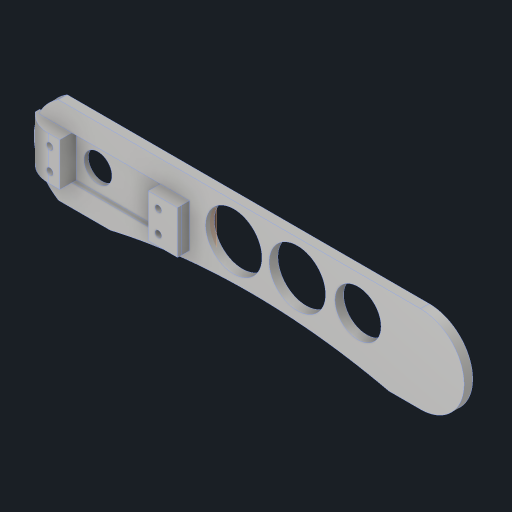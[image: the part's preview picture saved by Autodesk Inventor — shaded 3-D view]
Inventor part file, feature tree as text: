
AUTODESK INVENTOR PART (.ipt)
format: ipt  version: 2023.4 (Build 274418000, 418)  size: 249,344 bytes
history: native  units: mm
features: sketch x17, extrude x12, plane x1, fillet x1
ambient origin geometry x8: Origin, YZ Plane, XZ Plane, XY Plane, X Axis, Y Axis, Z Axis, Center Point
bodies: Solid1 (feature_tree)
feature tree (31):
  extrude  "Extrusion1"  Depth=20.0mm
  extrude  "Extrusion2"  Depth=4.0mm
  extrude  "Extrusion5"  Depth=11.9mm TaperAngle=0.0deg
  sketch  "Sketch6"  dims[d5=8.0mm d6=11.9mm d7=0.0mm]
  extrude  "Extrusion6"  Depth=10.0mm
  sketch  "Sketch8"  dims[d19=5.0mm d20=0.0mm d21=11.9mm d22=0.0mm]
  extrude  "Extrusion7"  Depth=11.9mm TaperAngle=0.0deg
  sketch  "Sketch9"  dims[d23=70.753mm d24=19.8mm]
  sketch  "Sketch10"  dims[d25=26.749mm d26=9.9mm]
  sketch  "Sketch11"  dims[d29=4.0mm d30=0.0mm d31=2.0mm d32=0.0mm d33=19.8mm]
  sketch  "Sketch12"  dims[d34=16.749mm d35=10.0mm]
  plane  "Work Plane1"
  extrude  "Extrusion9"  Depth=19.8mm
  extrude  "Extrusion10"  Depth=9.9mm
  extrude  "Extrusion11"  Depth=4.0mm TaperAngle=0.0deg
  fillet  "Fillet3"  Radius=19.8mm
  extrude  "Extrusion12"  Depth=10.0mm
  extrude  "Extrusion13"  Depth=19.8mm
  sketch  "Sketch17"  dims[d45=2.95mm]
  sketch  "Sketch18"  dims[d47=4.9mm]
  extrude  "Extrusion14"  Depth=7.5mm TaperAngle=0.0deg
  extrude  "Extrusion15"  Depth=5.5mm TaperAngle=0.0deg
  sketch  "Sketch20"  dims[d50=2.95mm d51=2.95mm d52=4.59mm d53=4.59mm d54=4.9mm d55=4.9mm d56=10.0mm d57=0.0mm d58=11.9mm d59=0.0mm d60=14.59mm d61=14.59mm d62=10.0mm d63=0.0mm]
  sketch  "Sketch1"  dims[d0=150.0mm d1=20.0mm]
  sketch  "Sketch5"  dims[d2=4.0mm d3=0.0mm d4=12.8mm]
  sketch  "Sketch7"  dims[d16=10.0mm d17=0.0mm d18=5.4mm]
  sketch  "Sketch13"  dims[d36=13.4mm d37=19.8mm]
  sketch  "Sketch14"  dims[d38=30.6mm d39=7.5mm d40=0.0mm]
  sketch  "Sketch15"  dims[d41=14.75mm d42=5.5mm d43=0.0mm]
  sketch  "Sketch16"  dims[d44=2.95mm]
  sketch  "Sketch19"  dims[d49=4.9mm]
